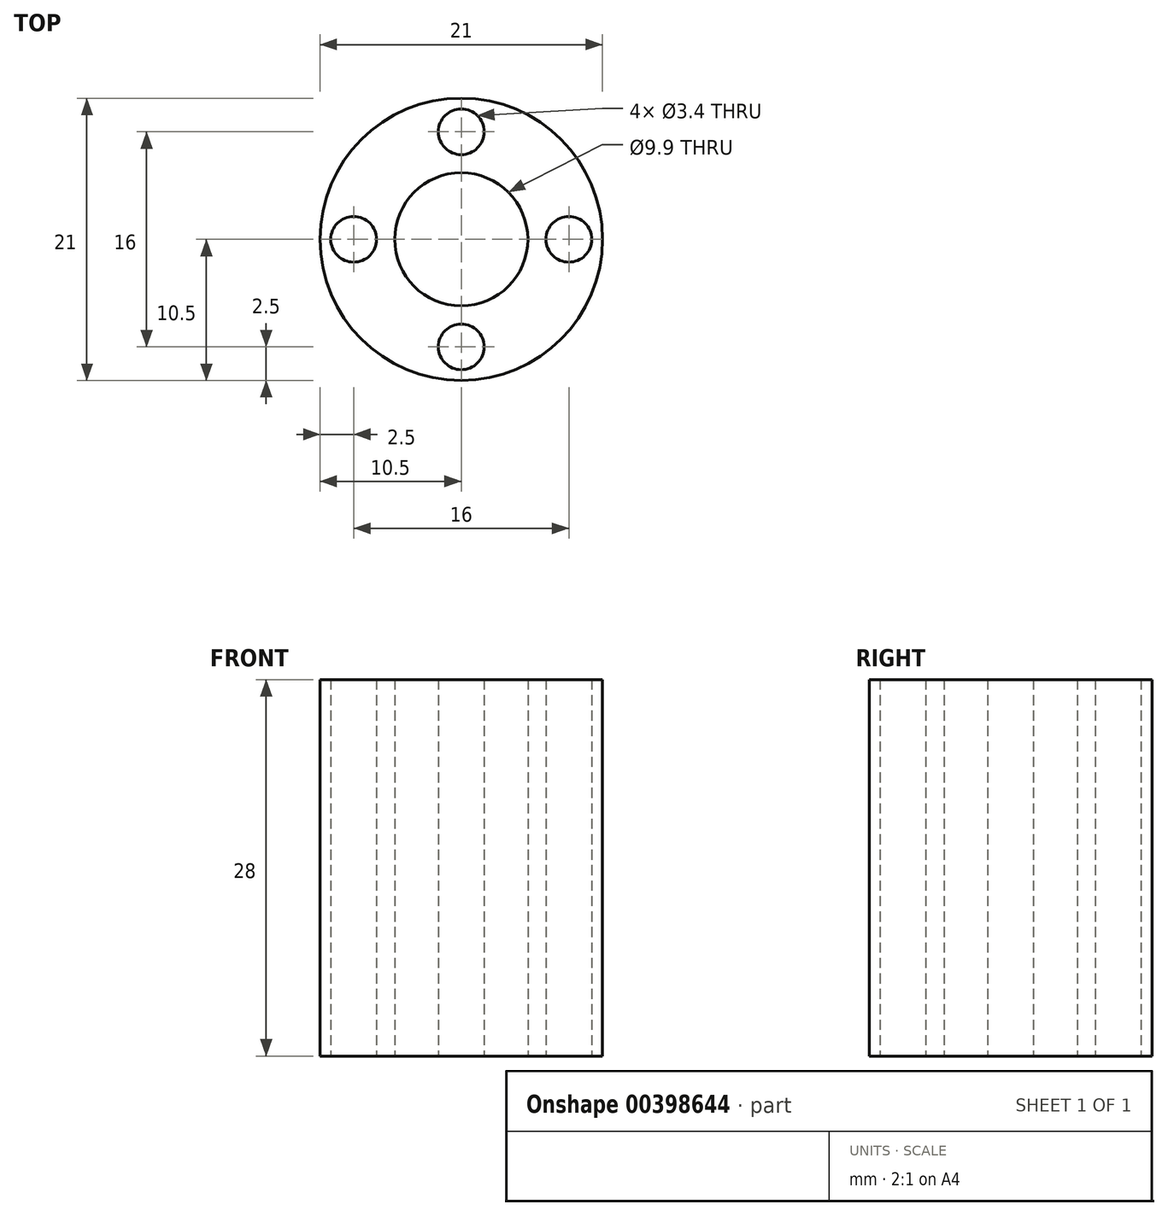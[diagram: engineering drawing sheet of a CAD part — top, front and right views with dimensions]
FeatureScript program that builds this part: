
annotation { "Feature Type Name" : "Feature", "Feature Type Description" : "" }
export const myFeature = defineFeature(function(context is Context, id is Id, definition is map)
    precondition{}
    {
        {
            var Q0;
            Q0=qCreatedBy(makeId("Top.planeOp"),FACE);
            var sketch = newSketch(context, id + "F0", { "sketchPlane" : qUnion([Q0])});
            skCircle(sketch, "E0", {"center": v(0, 0) * mm, "radius": 10.5 * mm});
            skCircle(sketch, "E1", {"center": v(-8, 0) * mm, "radius": 1.7 * mm});
            skCircle(sketch, "E2.MirrorC", {"center": v(8, 0) * mm, "radius": 1.7 * mm});
            skCircle(sketch, "E3", {"center": v(0, 8) * mm, "radius": 1.7 * mm});
            skCircle(sketch, "E4.MirrorC", {"center": v(0, -8) * mm, "radius": 1.7 * mm});
            skCircle(sketch, "E5", {"center": v(0, 0) * mm, "radius": 4.95 * mm});
            skSolve(sketch);
        }
        {
            var Q0;
            Q0 = qSketchRegion(id + "F0", true);
            extrude(context, id + "F1", {"entities" : qUnion([Q0]), "depth" : 28 * mm});
        }
    });
